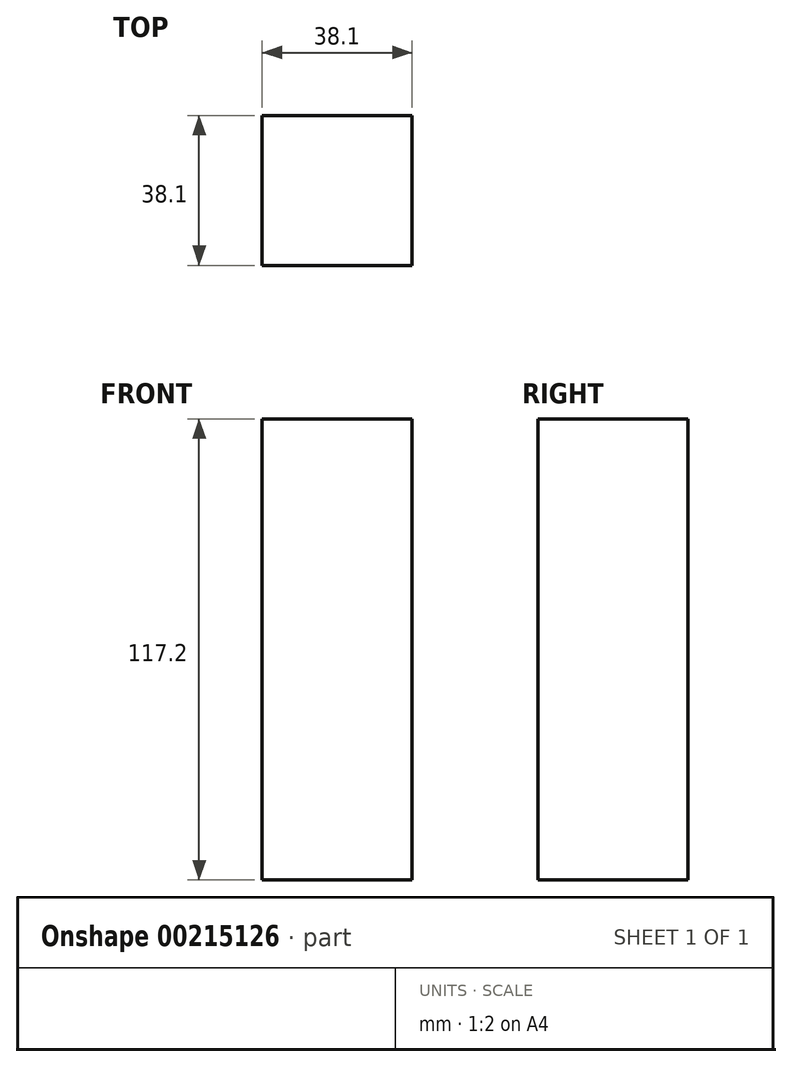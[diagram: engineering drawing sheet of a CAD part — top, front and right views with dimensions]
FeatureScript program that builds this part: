
annotation { "Feature Type Name" : "Feature", "Feature Type Description" : "" }
export const myFeature = defineFeature(function(context is Context, id is Id, definition is map)
    precondition{}
    {
        {
            var Q0;
            Q0=qCreatedBy(makeId("Top.planeOp"),FACE);
            var sketch = newSketch(context, id + "F0", { "sketchPlane" : qUnion([Q0])});
            skLineSegment(sketch, "E0.bottom", {"start": v(0, 0) * mm, "end": v(38.1, 0) * mm});
            skLineSegment(sketch, "E0.top", {"start": v(0, 38.1) * mm, "end": v(38.1, 38.1) * mm});
            skLineSegment(sketch, "E0.left", {"start": v(0, 0) * mm, "end": v(0, 38.1) * mm});
            skLineSegment(sketch, "E0.right", {"start": v(38.1, 0) * mm, "end": v(38.1, 38.1) * mm});
            skSolve(sketch);
        }
        {
            var Q0;
            Q0=makeQuery(id+"F0.imprint","IMPRINT",FACE,{"disambiguationData":[TD([[makeQuery(id+"F0.imprint","IMPRINT",EDGE,{"derivedFrom":sQuery(id+"F0.wireOp",EDGE,"E0.bottom")}),1.0]])]});
            extrude(context, id + "F1", {"entities" : qUnion([Q0]), "depth" : 117.2 * mm, "offsetDistance" : 25.4 * mm});
        }
    });
